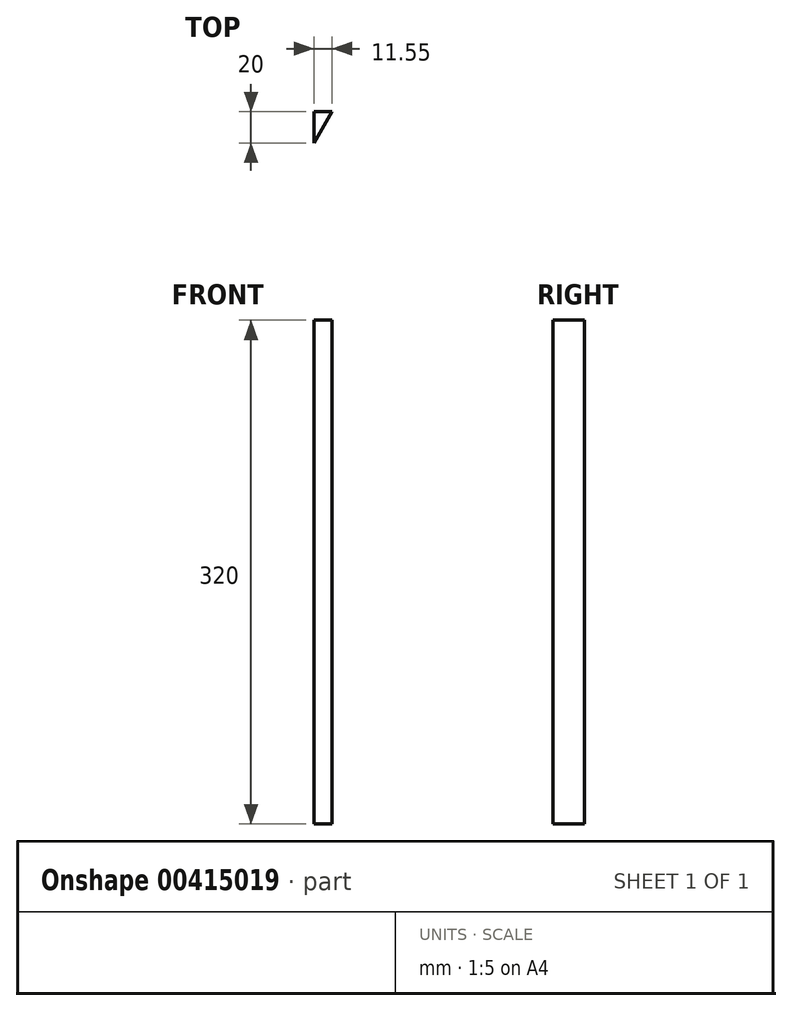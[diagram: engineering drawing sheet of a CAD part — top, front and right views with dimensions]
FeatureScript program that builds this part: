
annotation { "Feature Type Name" : "Feature", "Feature Type Description" : "" }
export const myFeature = defineFeature(function(context is Context, id is Id, definition is map)
    precondition{}
    {
        {
            var Q0;
            Q0=qCreatedBy(makeId("Top.planeOp"),FACE);
            var sketch = newSketch(context, id + "F0", { "sketchPlane" : qUnion([Q0])});
            skLineSegment(sketch, "E0", {"start": v(0, 0) * mm, "end": v(0, 20) * mm});
            skLineSegment(sketch, "E1", {"start": v(0, 20) * mm, "end": v(11.55, 20) * mm});
            skLineSegment(sketch, "E2", {"start": v(11.55, 20) * mm, "end": v(0, 0) * mm});
            skSolve(sketch);
        }
        {
            var Q0;
            Q0=makeQuery(id+"F0.imprint","IMPRINT",FACE,{"disambiguationData":[TD([[makeQuery(id+"F0.imprint","IMPRINT",EDGE,{"derivedFrom":sQuery(id+"F0.wireOp",EDGE,"E0")}),-1.0]])]});
            extrude(context, id + "F1", {"entities" : qUnion([Q0]), "depth" : 320 * mm});
        }
    });
